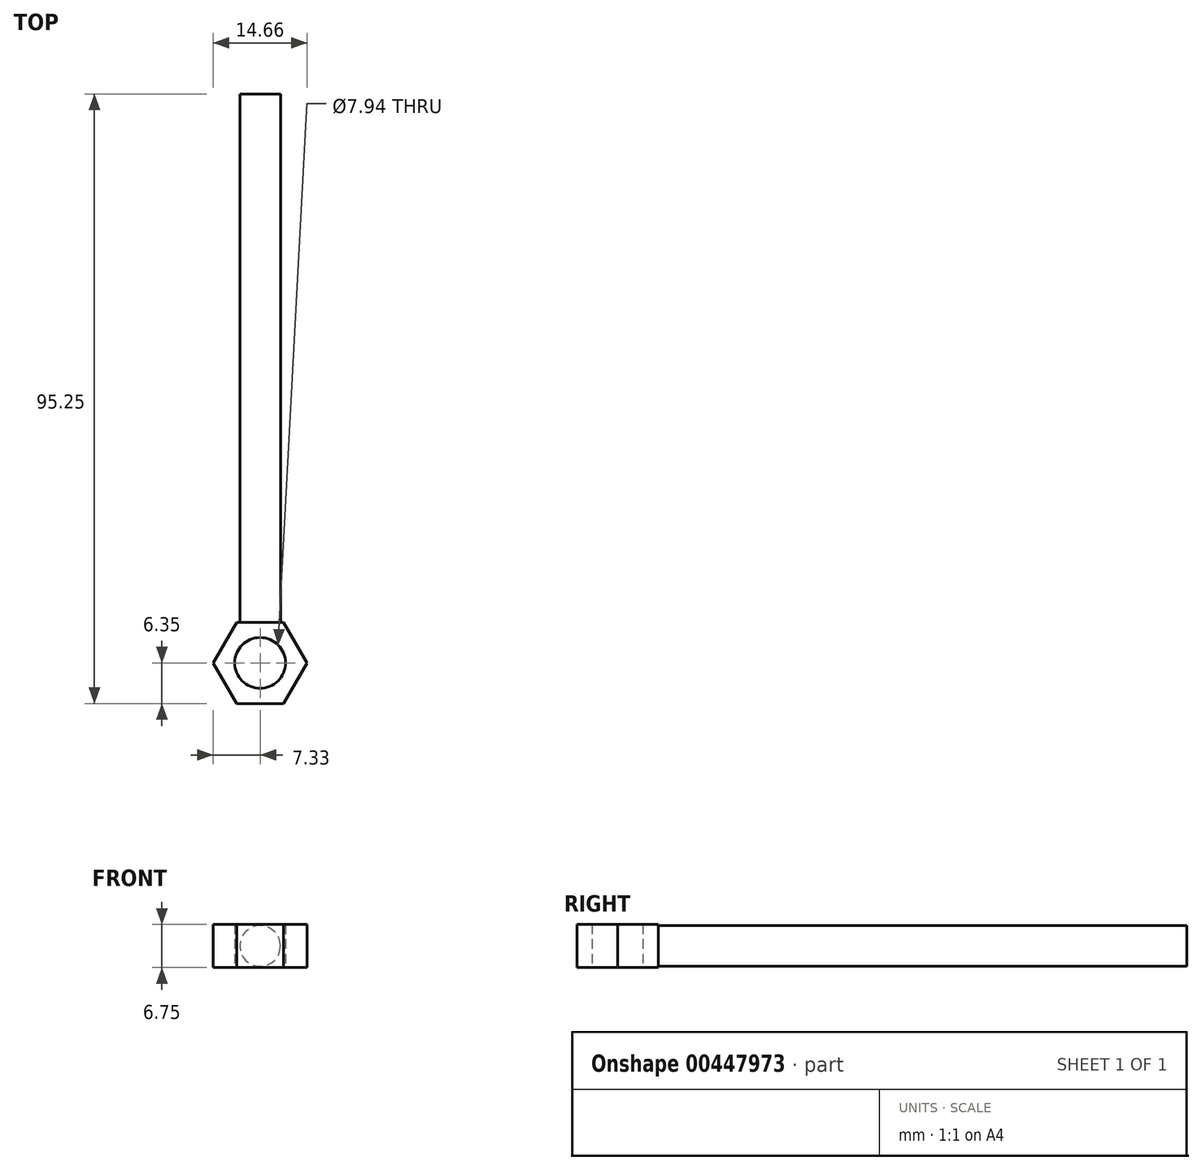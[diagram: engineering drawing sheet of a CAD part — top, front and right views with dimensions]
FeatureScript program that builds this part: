
annotation { "Feature Type Name" : "Feature", "Feature Type Description" : "" }
export const myFeature = defineFeature(function(context is Context, id is Id, definition is map)
    precondition{}
    {
        {
            var Q0;
            Q0=qCreatedBy(makeId("Top.planeOp"),FACE);
            var sketch = newSketch(context, id + "F0", { "sketchPlane" : qUnion([Q0])});
            skCircle(sketch, "E0", {"center": v(0, 0) * mm, "radius": 3.97 * mm});
            skCircle(sketch, "E1.cCircle", {"center": v(0, 0) * mm, "radius": 6.35 * mm, "construction": true});
            skLineSegment(sketch, "E1.0", {"start": v(-3.67, 6.35) * mm, "end": v(3.67, 6.35) * mm});
            skLineSegment(sketch, "E1.1", {"start": v(3.67, 6.35) * mm, "end": v(7.33, 0) * mm});
            skLineSegment(sketch, "E1.2", {"start": v(7.33, 0) * mm, "end": v(3.67, -6.35) * mm});
            skLineSegment(sketch, "E1.3", {"start": v(3.67, -6.35) * mm, "end": v(-3.67, -6.35) * mm});
            skLineSegment(sketch, "E1.4", {"start": v(-3.67, -6.35) * mm, "end": v(-7.33, 0) * mm});
            skLineSegment(sketch, "E1.5", {"start": v(-7.33, 0) * mm, "end": v(-3.67, 6.35) * mm});
            skPoint(sketch, "E1.0.midPoint", {"position": v(0, 6.35) * mm});
            skSolve(sketch);
        }
        {
            var Q0;
            Q0=makeQuery(id+"F0.imprint","IMPRINT",FACE,{"disambiguationData":[TD([[makeQuery(id+"F0.imprint","IMPRINT",EDGE,{"derivedFrom":sQuery(id+"F0.wireOp",EDGE,"E0")}),-1.0]])]});
            extrude(context, id + "F1", {"entities" : qUnion([Q0]), "depth" : 6.75 * mm});
        }
        {
            var Q0;
            Q0=makeQuery(id+"F1.opExtrude","SWEPT_FACE",FACE,{"disambiguationData":[OSD([sQuery(id+"F0.wireOp",EDGE,"E1.0")])]});
            var sketch = newSketch(context, id + "F2", { "sketchPlane" : qUnion([Q0])});
            skCircle(sketch, "E2", {"center": v(0, 3.37) * mm, "radius": 3.18 * mm});
            skPoint(sketch, "E2.centerSnap0", {"position": v(-3.67, 3.37) * mm});
            skSolve(sketch);
        }
        {
            var Q0;
            Q0=qSketchRegion(id+"F2",true);
            extrude(context, id + "F3", {"entities" : qUnion([Q0]), "operationType" : NewBodyOperationType.ADD, "depth" : 82.55 * mm});
        }
    });
